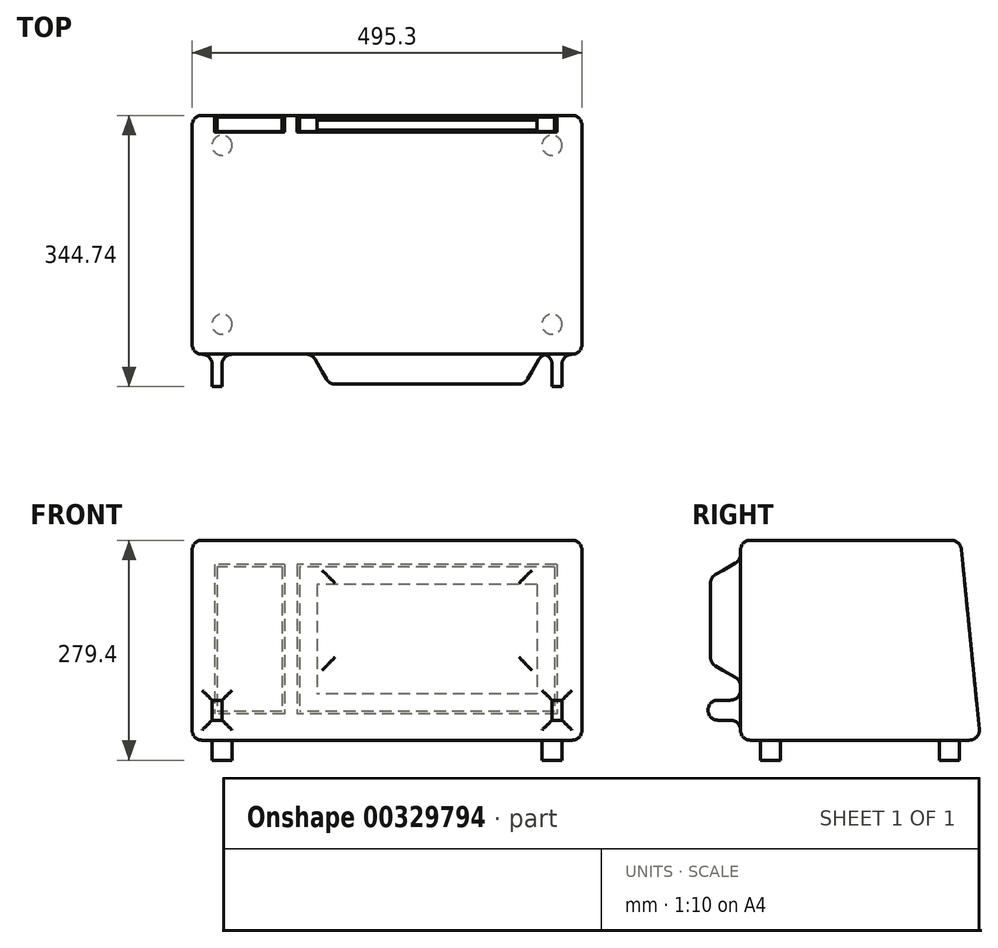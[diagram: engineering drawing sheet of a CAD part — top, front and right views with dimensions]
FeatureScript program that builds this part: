
annotation { "Feature Type Name" : "Feature", "Feature Type Description" : "" }
export const myFeature = defineFeature(function(context is Context, id is Id, definition is map)
    precondition{}
    {
        {
            var Q0;
            Q0=qCreatedBy(makeId("Right.planeOp"),FACE);
            var sketch = newSketch(context, id + "F0", { "sketchPlane" : qUnion([Q0])});
            skLineSegment(sketch, "E0.bottom", {"start": v(0, 0) * mm, "end": v(-304.8, 0) * mm});
            skLineSegment(sketch, "E0.top", {"start": v(-25.4, 254) * mm, "end": v(-304.8, 254) * mm});
            skLineSegment(sketch, "E0.left", {"start": v(0, 0) * mm, "end": v(-25.4, 254) * mm});
            skLineSegment(sketch, "E0.right", {"start": v(-304.8, 0) * mm, "end": v(-304.8, 254) * mm});
            skSolve(sketch);
        }
        {
            var Q0;
            Q0 = qSketchRegion(id + "F0", true);
            extrude(context, id + "F1", {"entities" : qUnion([Q0]), "depth" : 495.3 * mm});
        }
        {
            var Q0;
            Q0=makeQuery(id+"F1.opExtrude","SWEPT_FACE",FACE,{"disambiguationData":[OSD([sQuery(id+"F0.wireOp",EDGE,"E0.right")])]});
            var sketch = newSketch(context, id + "F2", { "sketchPlane" : qUnion([Q0])});
            skLineSegment(sketch, "E1.bottom", {"start": v(431.8, 228.6) * mm, "end": v(165.1, 228.6) * mm});
            skLineSegment(sketch, "E1.top", {"start": v(431.8, 76.2) * mm, "end": v(165.1, 76.2) * mm});
            skLineSegment(sketch, "E1.left", {"start": v(444.5, 215.9) * mm, "end": v(444.5, 88.9) * mm});
            skLineSegment(sketch, "E1.right", {"start": v(152.4, 215.9) * mm, "end": v(152.4, 88.9) * mm});
            skLineSegment(sketch, "E2.bottom", {"start": v(457.2, 50.8) * mm, "end": v(469.9, 50.8) * mm});
            skLineSegment(sketch, "E2.top", {"start": v(457.2, 25.4) * mm, "end": v(469.9, 25.4) * mm});
            skLineSegment(sketch, "E2.left", {"start": v(457.2, 50.8) * mm, "end": v(457.2, 25.4) * mm});
            skLineSegment(sketch, "E2.right", {"start": v(469.9, 50.8) * mm, "end": v(469.9, 25.4) * mm});
            skLineSegment(sketch, "E3.bottom", {"start": v(25.4, 50.8) * mm, "end": v(38.1, 50.8) * mm});
            skLineSegment(sketch, "E3.top", {"start": v(25.4, 25.4) * mm, "end": v(38.1, 25.4) * mm});
            skLineSegment(sketch, "E3.left", {"start": v(25.4, 50.8) * mm, "end": v(25.4, 25.4) * mm});
            skLineSegment(sketch, "E3.right", {"start": v(38.1, 50.8) * mm, "end": v(38.1, 25.4) * mm});
            skPoint(sketch, "E4.visualSharp", {"position": v(152.4, 228.6) * mm});
            skArc(sketch, "E4.filletArc", {"start": v(165.1, 228.6) * mm, "mid": v(156.12, 224.88) * mm, "end": v(152.4, 215.9) * mm});
            skPoint(sketch, "E5.visualSharp", {"position": v(444.5, 228.6) * mm});
            skArc(sketch, "E5.filletArc", {"start": v(444.5, 215.9) * mm, "mid": v(440.78, 224.88) * mm, "end": v(431.8, 228.6) * mm});
            skPoint(sketch, "E6.visualSharp", {"position": v(444.5, 76.2) * mm});
            skArc(sketch, "E6.filletArc", {"start": v(431.8, 76.2) * mm, "mid": v(440.78, 79.92) * mm, "end": v(444.5, 88.9) * mm});
            skPoint(sketch, "E7.visualSharp", {"position": v(152.4, 76.2) * mm});
            skArc(sketch, "E7.filletArc", {"start": v(152.4, 88.9) * mm, "mid": v(156.12, 79.92) * mm, "end": v(165.1, 76.2) * mm});
            skSolve(sketch);
        }
        {
            var Q0;
            Q0=makeQuery(id+"F2.imprint","IMPRINT",FACE,{"disambiguationData":[TD([[makeQuery(id+"F2.imprint","IMPRINT",EDGE,{"derivedFrom":sQuery(id+"F2.wireOp",EDGE,"E1.bottom")}),1.0]])]});
            extrude(context, id + "F3", {"entities" : qUnion([Q0]), "operationType" : NewBodyOperationType.ADD, "depth" : 38.1 * mm, "hasDraft" : true, "draftAngle" : 30 * degree, "draftPullDirection" : true});
        }
        {
            var Q0;
            Q0=makeQuery(id+"F2.imprint","IMPRINT",FACE,{"disambiguationData":[TD([[makeQuery(id+"F2.imprint","IMPRINT",EDGE,{"derivedFrom":sQuery(id+"F2.wireOp",EDGE,"E3.bottom")}),-1.0]])]});
            var Q1;
            Q1=makeQuery(id+"F2.imprint","IMPRINT",FACE,{"disambiguationData":[TD([[makeQuery(id+"F2.imprint","IMPRINT",EDGE,{"derivedFrom":sQuery(id+"F2.wireOp",EDGE,"E2.bottom")}),-1.0]])]});
            extrude(context, id + "F4", {"entities" : qUnion([Q0, Q1]), "operationType" : NewBodyOperationType.ADD, "depth" : 41.27 * mm});
        }
        {
            var Q0;
            Q0=makeQuery(id+"F4.opExtrude","CAP_EDGE",EDGE,{"disambiguationData":[OSD([sQuery(id+"F2.wireOp",EDGE,"E3.bottom")])],"isStart":false});
            var Q1;
            Q1=makeQuery(id+"F4.opExtrude","CAP_EDGE",EDGE,{"disambiguationData":[OSD([sQuery(id+"F2.wireOp",EDGE,"E3.top")])],"isStart":false});
            var Q2;
            Q2=makeQuery(id+"F4.opExtrude","CAP_EDGE",EDGE,{"disambiguationData":[OSD([sQuery(id+"F2.wireOp",EDGE,"E2.bottom")])],"isStart":false});
            var Q3;
            Q3=makeQuery(id+"F4.opExtrude","CAP_EDGE",EDGE,{"disambiguationData":[OSD([sQuery(id+"F2.wireOp",EDGE,"E2.top")])],"isStart":false});
            var Q4;
            Q4=makeQuery(id+"F3.opExtrude","CAP_FACE",FACE,{"disambiguationData":[OSD([sQuery(id+"F2.wireOp",EDGE,"E1.bottom"),sQuery(id+"F2.wireOp",EDGE,"E1.top"),sQuery(id+"F2.wireOp",EDGE,"E1.left"),sQuery(id+"F2.wireOp",EDGE,"E1.right"),sQuery(id+"F2.wireOp",EDGE,"E4.filletArc"),sQuery(id+"F2.wireOp",EDGE,"E5.filletArc"),sQuery(id+"F2.wireOp",EDGE,"E6.filletArc"),sQuery(id+"F2.wireOp",EDGE,"E7.filletArc")])],"isStart":false});
            var Q5;
            Q5=makeQuery(id+"F3.opExtrude","CAP_EDGE",EDGE,{"disambiguationData":[OSD([sQuery(id+"F2.wireOp",EDGE,"E1.bottom")])],"isStart":true});
            var Q6;
            Q6=makeQuery(id+"F1.opExtrude","SWEPT_FACE",FACE,{"disambiguationData":[OSD([sQuery(id+"F0.wireOp",EDGE,"E0.top")])]});
            var Q7;
            Q7=makeQuery(id+"F1.opExtrude","SWEPT_FACE",FACE,{"disambiguationData":[OSD([sQuery(id+"F0.wireOp",EDGE,"E0.right")])]});
            var Q8;
            Q8=makeQuery(id+"F1.opExtrude","CAP_FACE",FACE,{"disambiguationData":[OSD([sQuery(id+"F0.wireOp",EDGE,"E0.bottom"),sQuery(id+"F0.wireOp",EDGE,"E0.top"),sQuery(id+"F0.wireOp",EDGE,"E0.left"),sQuery(id+"F0.wireOp",EDGE,"E0.right")])],"isStart":false});
            var Q9;
            Q9=makeQuery(id+"F1.opExtrude","SWEPT_FACE",FACE,{"disambiguationData":[OSD([sQuery(id+"F0.wireOp",EDGE,"E0.left")])]});
            var Q10;
            Q10=makeQuery(id+"F1.opExtrude","CAP_FACE",FACE,{"disambiguationData":[OSD([sQuery(id+"F0.wireOp",EDGE,"E0.bottom"),sQuery(id+"F0.wireOp",EDGE,"E0.top"),sQuery(id+"F0.wireOp",EDGE,"E0.left"),sQuery(id+"F0.wireOp",EDGE,"E0.right")])],"isStart":true});
            fillet(context, id + "F5", {"entities" : qUnion([Q0, Q1, Q2, Q3, Q4, Q5, Q6, Q7, Q8, Q9, Q10]), "radius" : 12.7 * mm, "tangentPropagation" : true, "allowEdgeOverflow" : false});
        }
        {
            var Q0;
            Q0=makeQuery(id+"F1.opExtrude","SWEPT_FACE",FACE,{"disambiguationData":[OSD([sQuery(id+"F0.wireOp",EDGE,"E0.bottom")])]});
            var sketch = newSketch(context, id + "F6", { "sketchPlane" : qUnion([Q0])});
            skCircle(sketch, "E8", {"center": v(457.2, 39.43) * mm, "radius": 12.7 * mm});
            skCircle(sketch, "E9.0.1.0", {"center": v(457.2, 266.7) * mm, "radius": 12.7 * mm});
            skCircle(sketch, "E9.1.0.0", {"center": v(38.1, 39.43) * mm, "radius": 12.7 * mm});
            skCircle(sketch, "E9.1.1.0", {"center": v(38.1, 266.7) * mm, "radius": 12.7 * mm});
            skLineSegment(sketch, "E9.direction1", {"start": v(457.2, 39.43) * mm, "end": v(38.1, 39.43) * mm, "construction": true});
            skLineSegment(sketch, "E9.direction2", {"start": v(457.2, 39.43) * mm, "end": v(457.2, 266.7) * mm, "construction": true});
            skSolve(sketch);
        }
        {
            var Q0;
            Q0 = qSketchRegion(id + "F6", true);
            extrude(context, id + "F7", {"entities" : qUnion([Q0]), "operationType" : NewBodyOperationType.ADD, "depth" : 25.4 * mm});
        }
        {
            var Q0;
            Q0=makeQuery(id+"F1.opExtrude","SWEPT_FACE",FACE,{"disambiguationData":[OSD([sQuery(id+"F0.wireOp",EDGE,"E0.left")])]});
            var sketch = newSketch(context, id + "F8", { "sketchPlane" : qUnion([Q0])});
            skLineSegment(sketch, "E10.bottom", {"start": v(-463.55, 224.15) * mm, "end": v(-133.35, 224.15) * mm});
            skLineSegment(sketch, "E10.top", {"start": v(-463.55, 33.65) * mm, "end": v(-133.35, 33.65) * mm});
            skLineSegment(sketch, "E10.left", {"start": v(-463.55, 224.15) * mm, "end": v(-463.55, 33.65) * mm});
            skLineSegment(sketch, "E10.right", {"start": v(-133.35, 224.15) * mm, "end": v(-133.35, 33.65) * mm});
            skLineSegment(sketch, "E11.0", {"start": v(-460.38, 220.98) * mm, "end": v(-460.38, 36.83) * mm});
            skLineSegment(sketch, "E11.1", {"start": v(-460.38, 220.98) * mm, "end": v(-136.52, 220.98) * mm});
            skLineSegment(sketch, "E11.2", {"start": v(-136.52, 220.98) * mm, "end": v(-136.52, 36.83) * mm});
            skLineSegment(sketch, "E11.3", {"start": v(-460.38, 36.83) * mm, "end": v(-136.52, 36.83) * mm});
            skLineSegment(sketch, "E12.bottom", {"start": v(-438.15, 198.75) * mm, "end": v(-158.75, 198.75) * mm});
            skLineSegment(sketch, "E12.top", {"start": v(-438.15, 59.05) * mm, "end": v(-158.75, 59.05) * mm});
            skLineSegment(sketch, "E12.left", {"start": v(-438.15, 198.75) * mm, "end": v(-438.15, 59.05) * mm});
            skLineSegment(sketch, "E12.right", {"start": v(-158.75, 198.75) * mm, "end": v(-158.75, 59.05) * mm});
            skLineSegment(sketch, "E13.bottom", {"start": v(-117.47, 224.15) * mm, "end": v(-28.58, 224.15) * mm});
            skLineSegment(sketch, "E13.top", {"start": v(-117.47, 33.65) * mm, "end": v(-28.57, 33.65) * mm});
            skLineSegment(sketch, "E13.left", {"start": v(-117.47, 224.15) * mm, "end": v(-117.47, 33.65) * mm});
            skLineSegment(sketch, "E13.right", {"start": v(-28.57, 224.15) * mm, "end": v(-28.57, 33.65) * mm});
            skLineSegment(sketch, "E14.0", {"start": v(-114.3, 220.98) * mm, "end": v(-114.3, 36.83) * mm});
            skLineSegment(sketch, "E14.1", {"start": v(-114.3, 220.98) * mm, "end": v(-31.75, 220.98) * mm});
            skLineSegment(sketch, "E14.2", {"start": v(-31.75, 220.98) * mm, "end": v(-31.75, 36.83) * mm});
            skLineSegment(sketch, "E14.3", {"start": v(-114.3, 36.83) * mm, "end": v(-31.75, 36.83) * mm});
            skSolve(sketch);
        }
        {
            var Q0;
            Q0=makeQuery(id+"F8.imprint","IMPRINT",FACE,{"disambiguationData":[TD([[makeQuery(id+"F8.imprint","IMPRINT",EDGE,{"derivedFrom":sQuery(id+"F8.wireOp",EDGE,"E12.bottom")}),-1.0]])]});
            var Q1;
            Q1=makeQuery(id+"F8.imprint","IMPRINT",FACE,{"disambiguationData":[TD([[makeQuery(id+"F8.imprint","IMPRINT",EDGE,{"derivedFrom":sQuery(id+"F8.wireOp",EDGE,"E10.bottom")}),-1.0]])]});
            var Q2;
            Q2=makeQuery(id+"F8.imprint","IMPRINT",FACE,{"disambiguationData":[TD([[makeQuery(id+"F8.imprint","IMPRINT",EDGE,{"derivedFrom":sQuery(id+"F8.wireOp",EDGE,"E13.bottom")}),-1.0]])]});
            extrude(context, id + "F9", {"entities" : qUnion([Q0, Q1, Q2]), "operationType" : NewBodyOperationType.REMOVE, "oppositeDirection" : true, "depth" : 1.27 * mm});
        }
    });
